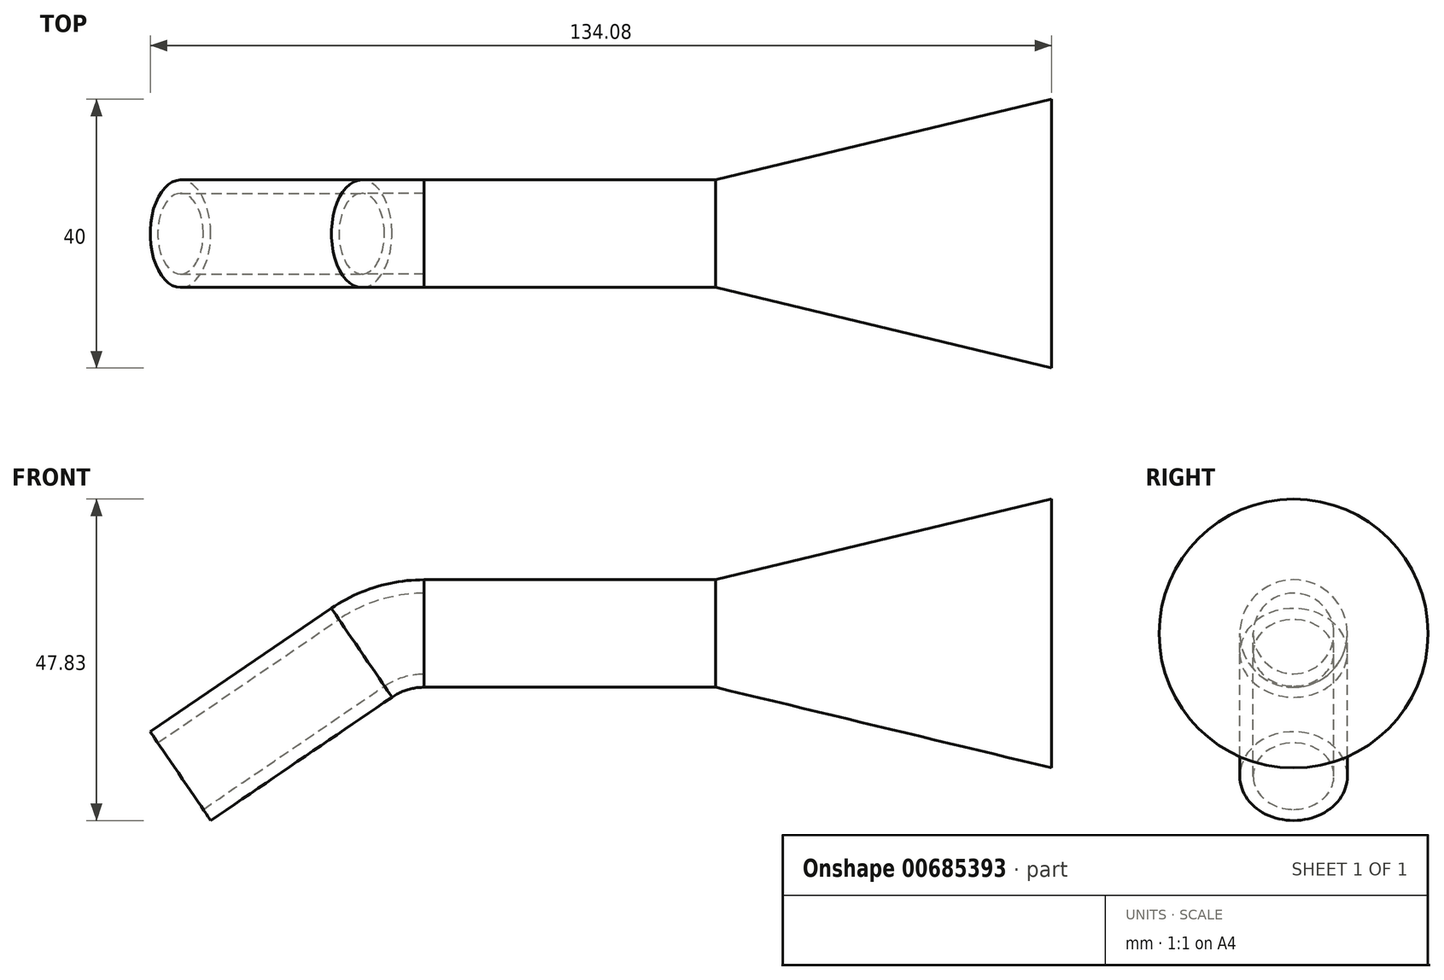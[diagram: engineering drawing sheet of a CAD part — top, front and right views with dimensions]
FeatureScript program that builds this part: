
annotation { "Feature Type Name" : "Feature", "Feature Type Description" : "" }
export const myFeature = defineFeature(function(context is Context, id is Id, definition is map)
    precondition{}
    {
        {
            var Q0;
            Q0=qCreatedBy(makeId("Front.planeOp"),FACE);
            var sketch = newSketch(context, id + "F0", { "sketchPlane" : qUnion([Q0])});
            skLineSegment(sketch, "E0", {"start": v(0, 0) * mm, "end": v(-50, 0) * mm});
            skLineSegment(sketch, "E1", {"start": v(0, 20) * mm, "end": v(0, 0) * mm});
            skLineSegment(sketch, "E2", {"start": v(0, 20) * mm, "end": v(-50, 8) * mm});
            skLineSegment(sketch, "E3", {"start": v(-50, 8) * mm, "end": v(-50, 0) * mm});
            skLineSegment(sketch, "E4", {"start": v(0, 0) * mm, "end": v(0, 16) * mm});
            skLineSegment(sketch, "E5", {"start": v(0, 16) * mm, "end": v(-50, 6) * mm});
            skLineSegment(sketch, "E6", {"start": v(-50, 6) * mm, "end": v(-50, 0) * mm});
            skLineSegment(sketch, "E7", {"start": v(-50, 8) * mm, "end": v(-93.33, 8) * mm});
            skLineSegment(sketch, "E8", {"start": v(-93.33, 8) * mm, "end": v(-93.33, 0) * mm});
            skLineSegment(sketch, "E9", {"start": v(-93.33, 0) * mm, "end": v(-50, 0) * mm});
            skLineSegment(sketch, "E10", {"start": v(-50, 0) * mm, "end": v(-50, 6) * mm});
            skLineSegment(sketch, "E11", {"start": v(-93.33, 6) * mm, "end": v(-93.33, 0) * mm});
            skLineSegment(sketch, "E12", {"start": v(-50, 0) * mm, "end": v(-93.33, 0) * mm});
            skLineSegment(sketch, "E13", {"start": v(-93.33, 6) * mm, "end": v(-50, 6) * mm});
            skArc(sketch, "E14", {"start": v(-93.33, 8) * mm, "mid": v(-100.55, 6.91) * mm, "end": v(-107.12, 3.75) * mm});
            skLineSegment(sketch, "E15", {"start": v(-107.12, 3.75) * mm, "end": v(-134.08, -14.6) * mm});
            skLineSegment(sketch, "E16.0", {"start": v(-106, 2.1) * mm, "end": v(-132.96, -16.26) * mm});
            skArc(sketch, "E16.1", {"start": v(-93.33, 6) * mm, "mid": v(-99.96, 5) * mm, "end": v(-106, 2.1) * mm});
            skLineSegment(sketch, "E17.0", {"start": v(-102.62, -2.86) * mm, "end": v(-129.58, -21.22) * mm});
            skArc(sketch, "E17.1", {"start": v(-93.33, 0) * mm, "mid": v(-98.2, -0.73) * mm, "end": v(-102.62, -2.86) * mm});
            skLineSegment(sketch, "E18", {"start": v(-129.58, -21.22) * mm, "end": v(-132.96, -16.26) * mm});
            skLineSegment(sketch, "E19", {"start": v(-132.96, -16.26) * mm, "end": v(-134.08, -14.6) * mm});
            skLineSegment(sketch, "E20", {"start": v(-107.12, 3.75) * mm, "end": v(-106, 2.1) * mm});
            skLineSegment(sketch, "E21", {"start": v(-106, 2.1) * mm, "end": v(-102.62, -2.86) * mm});
            skSolve(sketch);
        }
        {
            var Q0;
            Q0=makeQuery(id+"F0.imprint","IMPRINT",FACE,{"disambiguationData":[TD([[makeQuery(id+"F0.imprint","IMPRINT",EDGE,{"derivedFrom":sQuery(id+"F0.wireOp",EDGE,"E3")}),-1.0]])]});
            var Q1;
            Q1=makeQuery(id+"F0.imprint","IMPRINT",FACE,{"disambiguationData":[TD([[makeQuery(id+"F0.imprint","IMPRINT",EDGE,{"derivedFrom":sQuery(id+"F0.wireOp",EDGE,"E1")}),-1.0]])]});
            var Q2;
            Q2=sQuery(id+"F0.wireOp",EDGE,"E0");
            revolve(context, id + "F1", {"entities" : qUnion([Q0, Q1]), "axis" : qUnion([Q2]), "revolveType" : RevolveType.FULL});
        }
        {
            var Q0;
            Q0=makeQuery(id+"F0.imprint","IMPRINT",FACE,{"disambiguationData":[TD([[makeQuery(id+"F0.imprint","IMPRINT",EDGE,{"derivedFrom":sQuery(id+"F0.wireOp",EDGE,"E15")}),1.0]])]});
            var Q1;
            Q1=sQuery(id+"F0.wireOp",EDGE,"E17.0");
            revolve(context, id + "F2", {"entities" : qUnion([Q0]), "axis" : qUnion([Q1]), "revolveType" : RevolveType.FULL});
        }
        {
            var Q0;
            Q0=makeQuery(id+"F1.opRevolve","SWEPT_FACE",FACE,{"disambiguationData":[OSD([sQuery(id+"F0.wireOp",EDGE,"E8")])]});
            var Q1;
            Q1=makeQuery(id+"F2.opRevolve","SWEPT_FACE",FACE,{"disambiguationData":[OSD([sQuery(id+"F0.wireOp",EDGE,"E20")])]});
            var Q2;
            Q2=sQuery(id+"F0.wireOp",EDGE,"E17.1");
            sweep(context, id + "F3", {"profiles" : qUnion([Q0, Q1]), "path" : qUnion([Q2])});
        }
    });
